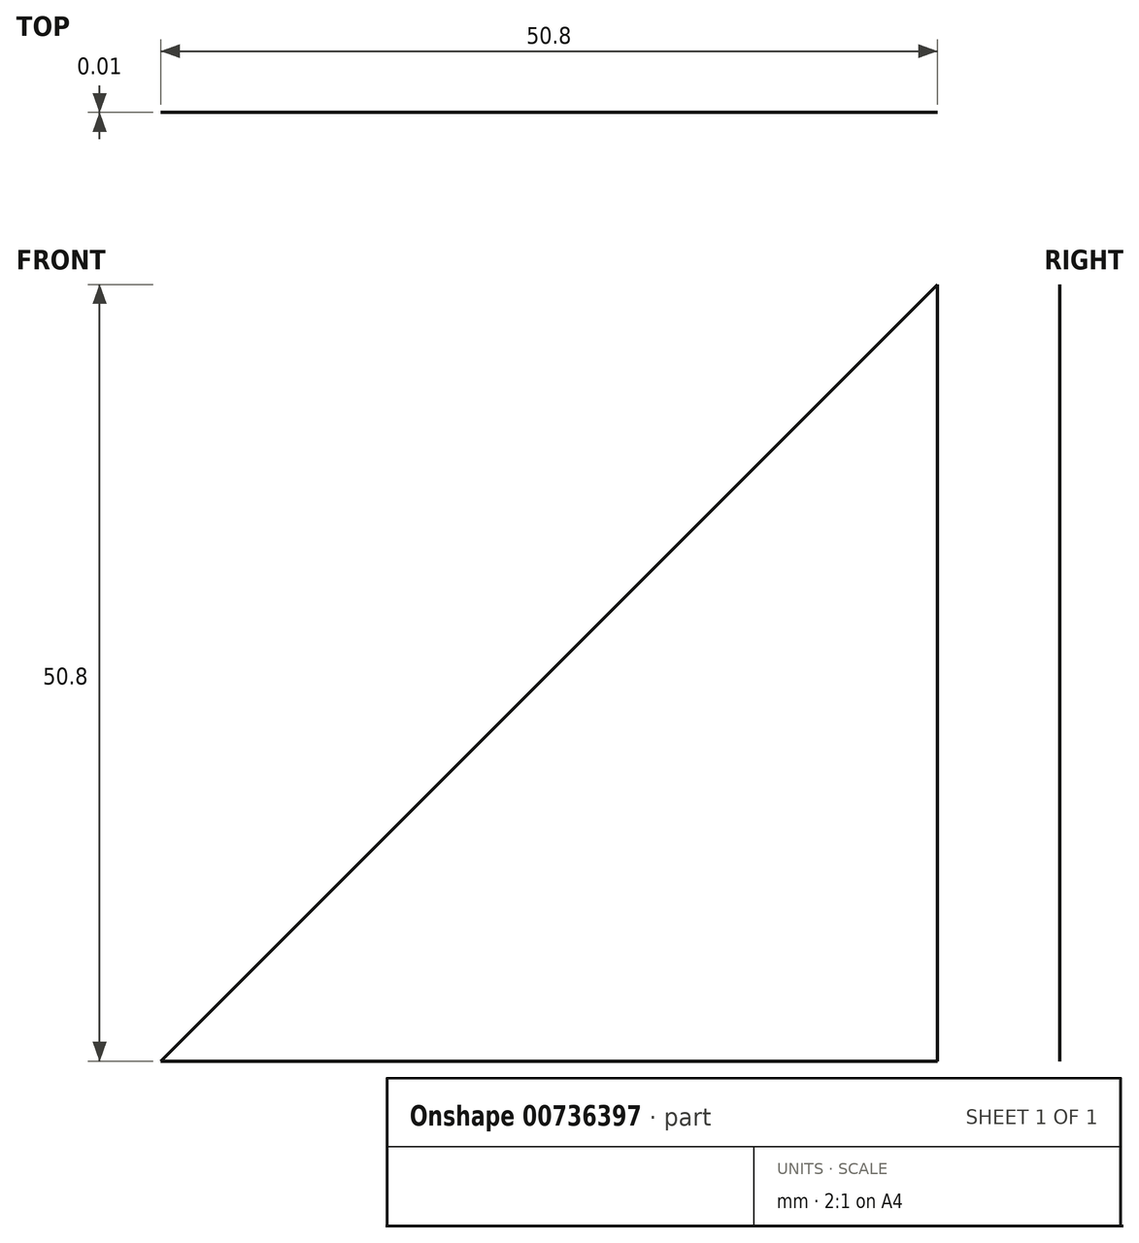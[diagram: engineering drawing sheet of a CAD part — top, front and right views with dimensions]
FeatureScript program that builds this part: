
annotation { "Feature Type Name" : "Feature", "Feature Type Description" : "" }
export const myFeature = defineFeature(function(context is Context, id is Id, definition is map)
    precondition{}
    {
        {
            var Q0;
            Q0=qCreatedBy(makeId("Front.planeOp"),FACE);
            var sketch = newSketch(context, id + "F0", { "sketchPlane" : qUnion([Q0])});
            skLineSegment(sketch, "E0.bottom", {"start": v(0, 0) * mm, "end": v(50.8, 0) * mm});
            skLineSegment(sketch, "E0.right", {"start": v(50.8, 0) * mm, "end": v(50.8, 50.8) * mm});
            skLineSegment(sketch, "E1", {"start": v(0, 0) * mm, "end": v(50.8, 50.8) * mm});
            skSolve(sketch);
        }
        {
            var Q0;
            Q0=makeQuery(id+"F0.imprint","IMPRINT",FACE,{"disambiguationData":[TD([[makeQuery(id+"F0.imprint","IMPRINT",EDGE,{"derivedFrom":sQuery(id+"F0.wireOp",EDGE,"E0.bottom")}),1.0]])]});
            extrude(context, id + "F1", {"entities" : qUnion([Q0]), "depth" : 3 / 406.4 * mm, "offsetDistance" : 25.4 * mm});
        }
    });
